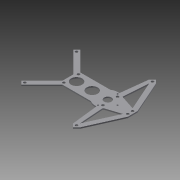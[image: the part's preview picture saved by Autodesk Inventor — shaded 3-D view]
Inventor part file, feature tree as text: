
AUTODESK INVENTOR PART (.ipt)
format: ipt  version: 2013 (Build 170138000, 138)  size: 228,864 bytes
history: native  units: in
note: dims shown in document units (in); Inventor stores cm internally (conversion verified against a paired STEP export)
features: extrude x7, sketch x7, reference x2
ambient origin geometry x8: Origin, YZ Plane, XZ Plane, XY Plane, X Axis, Y Axis, Z Axis, Center Point
feature tree (16):
  extrude  "Extrusion3"  Depth=0.748in
  extrude  "Extrusion4"  Depth=1.6in
  extrude  "Extrusion5"  Depth=1.125in
  extrude  "Extrusion6"  Depth=0.125in TaperAngle=0.0deg
  extrude  "Extrusion7"  Depth=0.266in
  sketch  "Sketch6"  dims[d21=0.25in d22=0.25in]
  extrude  "Extrusion9"  Depth=0.25in
  extrude  "Extrusion10"  Depth=0.25in
  sketch  "Sketch1"  dims[d3=2.0in d4=0.748in]
  sketch  "Sketch2"  dims[d12=1.125in d13=1.6in]
  sketch  "Sketch3"  dims[d14=4.5in d15=1.125in]
  sketch  "Sketch4"  dims[d16=1.6in d17=0.125in d18=0.0in]
  reference  "Reference1"
  sketch  "Sketch5"  dims[d19=0.266in d20=0.266in]
  sketch  "Sketch7"  dims[d23=0.25in d24=0.25in d25=1.0in d26=0.0in d27=0.266in d28=0.266in d29=0.25in d30=0.25in d31=0.25in d32=0.25in d33=1.0in d34=0.0in d35=0.25in d36=0.125in d39=0.5in d40=0.5in d41=0.125in d42=0.0in d47=2.375in d48=0.125in d49=0.0in d56=0.8in d57=1.0in d58=1.0in d59=1.0in d60=0.125in d61=0.0in d62=1.0in d63=0.0in]
  reference  "Reference2"
